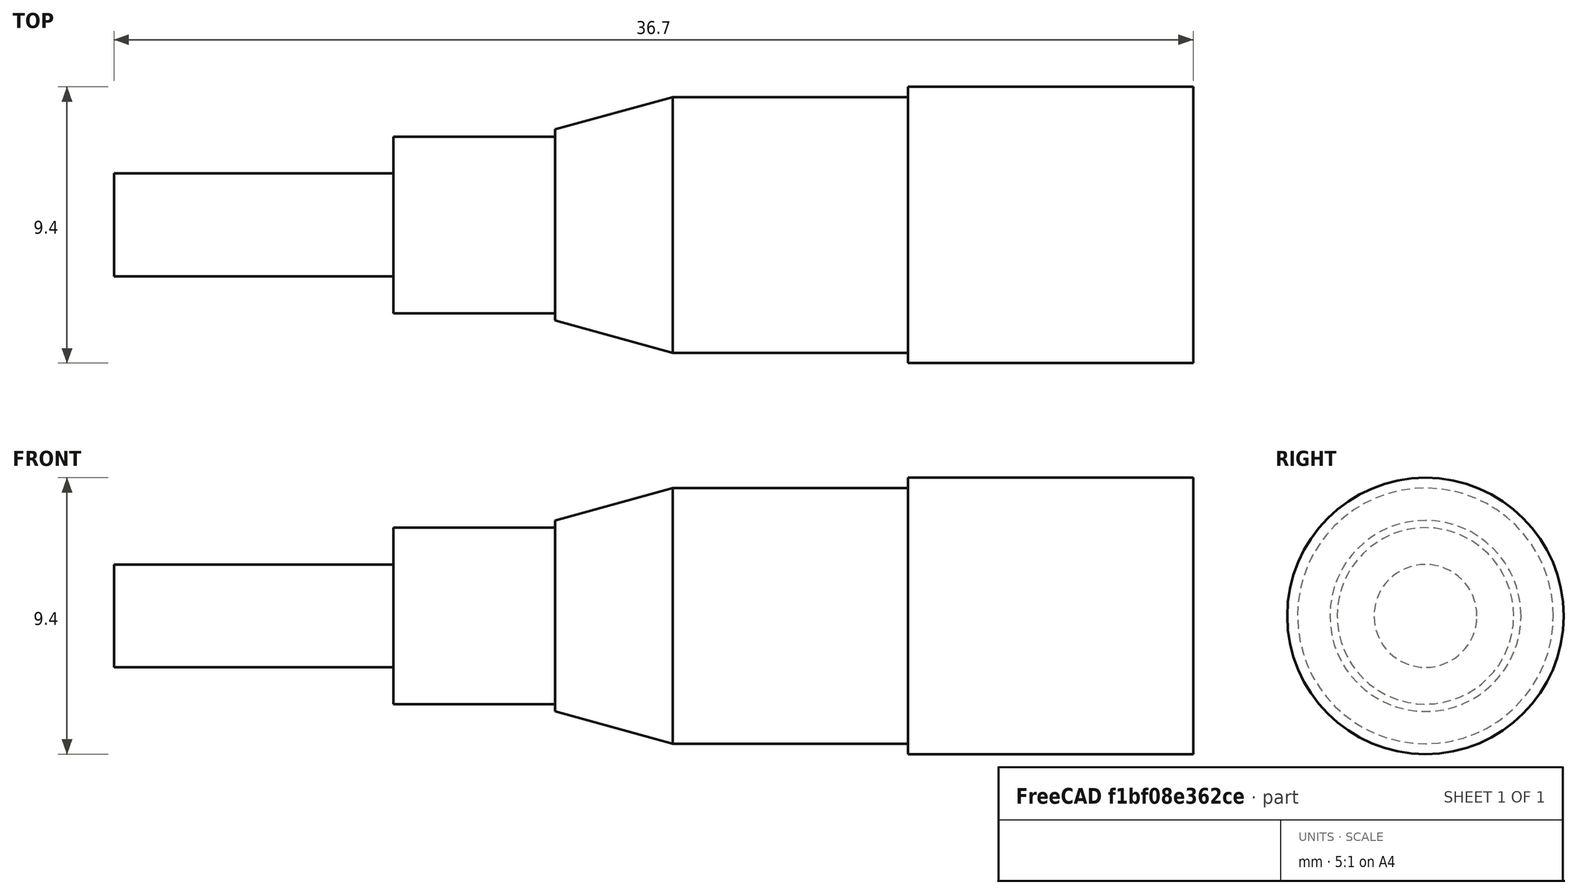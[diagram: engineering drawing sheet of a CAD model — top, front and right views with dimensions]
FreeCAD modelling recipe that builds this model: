
FCSTD DOCUMENT  (FreeCAD 0.19R)
Label: MicrometerModel
License: All rights reserved
LicenseURL: http://en.wikipedia.org/wiki/All_rights_reserved
objects: Sketcher::SketchObject×1, PartDesign::Revolution×1, PartDesign::Body×1, Mesh::Feature×1
note: 4 computed .brp shape members not serialized (recipe doc carries the construction recipe); baked Part::Feature solids carry a one-line shape summary decoded from their .brp

FEATURE [Sketcher::SketchObject] Sketch
  FullyConstrained = true
  MapMode = 5
  Placement = pos=(0,0,0) rot=(1,0,0;1.5708rad)
  Support = -> [XZ_Plane]
  sketch-geometry (11):
    g0: LineSegment StartX=0 StartY=0 StartZ=0 EndX=0 EndY=1.75 EndZ=0
    g1: LineSegment StartX=0 StartY=1.75 StartZ=0 EndX=9.5 EndY=1.75 EndZ=0
    g2: LineSegment StartX=9.5 StartY=1.75 StartZ=0 EndX=9.5 EndY=3 EndZ=0
    g3: LineSegment StartX=9.5 StartY=3 StartZ=0 EndX=15 EndY=3 EndZ=0
    g4: LineSegment StartX=15 StartY=3 StartZ=0 EndX=15 EndY=3.25 EndZ=0
    g5: LineSegment StartX=15 StartY=3.25 StartZ=0 EndX=19 EndY=4.35 EndZ=0
    g6: LineSegment StartX=19 StartY=4.35 StartZ=0 EndX=27 EndY=4.35 EndZ=0
    g7: LineSegment StartX=27 StartY=4.35 StartZ=0 EndX=27 EndY=4.7 EndZ=0
    g8: LineSegment StartX=27 StartY=4.7 StartZ=0 EndX=36.7 EndY=4.7 EndZ=0
    g9: LineSegment StartX=36.7 StartY=4.7 StartZ=0 EndX=36.7 EndY=0 EndZ=0
    g10: LineSegment StartX=36.7 StartY=0 StartZ=0 EndX=0 EndY=0 EndZ=0
  constraints (32):
    c: Coincident(g-1,g0)
    c: PointOnObject(g0,g-2)
    c: Coincident(g0,g1)
    c: Horizontal(g1)
    c: Coincident(g1,g2)
    c: Coincident(g2,g3)
    c: Horizontal(g3)
    c: Coincident(g3,g4)
    c: Vertical(g4)
    c: Coincident(g5,g6)
    c: Horizontal(g6)
    c: Coincident(g6,g7)
    c: Coincident(g7,g8)
    c: Horizontal(g8)
    c: Coincident(g8,g9)
    c: Vertical(g9)
    c: Coincident(g9,g10)
    c: Coincident(g10,g0)
    c: Horizontal(g10)
    c: DistanceY(g0,g0) = 1.75
    c: DistanceY(g2) = 3
    c: DistanceY(g4) = 3.25
    c: DistanceY(g5) = 4.35
    c: DistanceY(g7) = 4.7
    c: DistanceX(g1,g1) = 9.5
    c: Vertical(g2)
    c: Distance(g3) = 5.5
    c: DistanceX(g9) = 36.7
    c: Coincident(g5,g4)
    c: Vertical(g7)
    c: DistanceX(g6) = 27
    c: DistanceX(g5) = 19
FEATURE [PartDesign::Revolution] Revolution
  Angle = 360
  Axis = (1,0,0)
  Base = (0,0,0)
  Placement = pos=(0,0,0) rot=(1,0,0;1.5708rad)
  Profile = -> Sketch
  ReferenceAxis = -> Sketch [H_Axis]
FEATURE [PartDesign::Body] Body
  Group = -> [Sketch,Revolution]
  Origin = -> Origin
  Tip = -> Revolution
FEATURE [Mesh::Feature] Mesh  label="Revolution (Meshed)"
